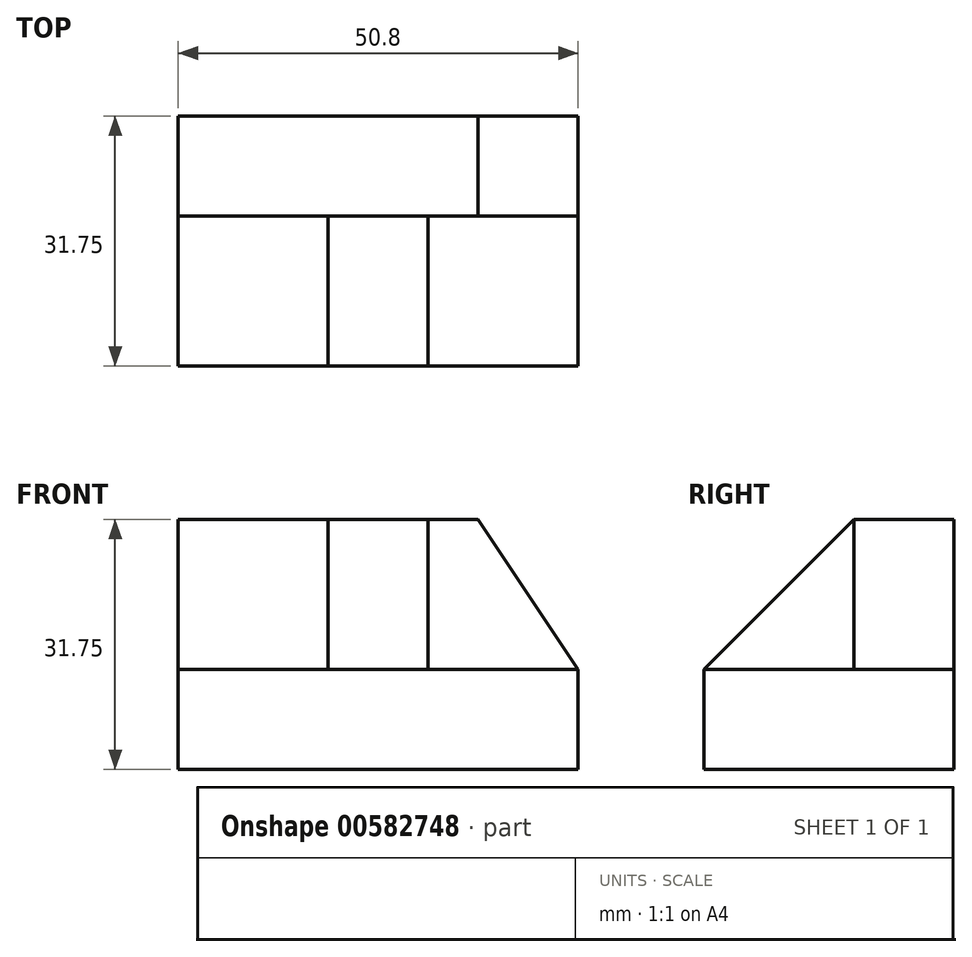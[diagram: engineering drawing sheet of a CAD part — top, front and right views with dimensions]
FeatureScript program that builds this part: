
annotation { "Feature Type Name" : "Feature", "Feature Type Description" : "" }
export const myFeature = defineFeature(function(context is Context, id is Id, definition is map)
    precondition{}
    {
        {
            var Q0;
            Q0=qCreatedBy(makeId("Right.planeOp"),FACE);
            var sketch = newSketch(context, id + "F0", { "sketchPlane" : qUnion([Q0])});
            skLineSegment(sketch, "E0", {"start": v(53.4, 52.7) * mm, "end": v(53.4, 20.95) * mm});
            skLineSegment(sketch, "E1", {"start": v(53.4, 20.95) * mm, "end": v(21.64, 20.95) * mm});
            skLineSegment(sketch, "E2", {"start": v(21.64, 20.95) * mm, "end": v(21.64, 33.65) * mm});
            skLineSegment(sketch, "E3", {"start": v(21.64, 33.65) * mm, "end": v(40.7, 33.65) * mm});
            skLineSegment(sketch, "E4", {"start": v(40.7, 33.65) * mm, "end": v(40.7, 52.7) * mm});
            skLineSegment(sketch, "E5", {"start": v(40.7, 52.7) * mm, "end": v(53.4, 52.7) * mm});
            skSolve(sketch);
        }
        {
            var Q0;
            Q0 = qSketchRegion(id + "F0", true);
            extrude(context, id + "F1", {"entities" : qUnion([Q0]), "depth" : 50.8 * mm, "offsetDistance" : 25.4 * mm});
        }
        {
            var Q0;
            Q0=makeQuery(id+"F1.opExtrude","SWEPT_FACE",FACE,{"disambiguationData":[OSD([sQuery(id+"F0.wireOp",EDGE,"E4")])]});
            var sketch = newSketch(context, id + "F2", { "sketchPlane" : qUnion([Q0])});
            skLineSegment(sketch, "E6", {"start": v(38.1, 52.7) * mm, "end": v(50.8, 33.65) * mm});
            skLineSegment(sketch, "E7", {"start": v(50.8, 33.65) * mm, "end": v(50.8, 52.7) * mm});
            skLineSegment(sketch, "E8", {"start": v(50.8, 52.7) * mm, "end": v(38.1, 52.7) * mm});
            skSolve(sketch);
        }
        {
            var Q0;
            Q0 = qSketchRegion(id + "F2", true);
            extrude(context, id + "F3", {"entities" : qUnion([Q0]), "operationType" : NewBodyOperationType.REMOVE, "oppositeDirection" : true, "depth" : 12.7 * mm, "offsetDistance" : 25.4 * mm});
        }
        {
            var Q0;
            Q0=makeQuery(id+"F1.opExtrude","CAP_FACE",FACE,{"disambiguationData":[OSD([sQuery(id+"F0.wireOp",EDGE,"E0"),sQuery(id+"F0.wireOp",EDGE,"E1"),sQuery(id+"F0.wireOp",EDGE,"E2"),sQuery(id+"F0.wireOp",EDGE,"E3"),sQuery(id+"F0.wireOp",EDGE,"E4"),sQuery(id+"F0.wireOp",EDGE,"E5")])],"isStart":true});
            var sketch = newSketch(context, id + "F4", { "sketchPlane" : qUnion([Q0])});
            skLineSegment(sketch, "E9", {"start": v(-40.7, 52.7) * mm, "end": v(-21.64, 33.65) * mm});
            skLineSegment(sketch, "E10", {"start": v(-21.64, 33.65) * mm, "end": v(-40.7, 33.65) * mm});
            skLineSegment(sketch, "E11", {"start": v(-40.7, 33.65) * mm, "end": v(-40.7, 52.7) * mm});
            skSolve(sketch);
        }
        {
            var Q0;
            Q0 = qSketchRegion(id + "F4", true);
            extrude(context, id + "F5", {"entities" : qUnion([Q0]), "oppositeDirection" : true, "depth" : 31.75 * mm, "offsetDistance" : 25.4 * mm});
        }
        {
            var Q0;
            Q0=makeQuery(id+"F5.opExtrude","CAP_FACE",FACE,{"disambiguationData":[OSD([sQuery(id+"F4.wireOp",EDGE,"E9"),sQuery(id+"F4.wireOp",EDGE,"E10"),sQuery(id+"F4.wireOp",EDGE,"E11")])],"isStart":true});
            var sketch = newSketch(context, id + "F6", { "sketchPlane" : qUnion([Q0])});
            skLineSegment(sketch, "E12", {"start": v(-40.7, 52.7) * mm, "end": v(-40.7, 33.65) * mm});
            skLineSegment(sketch, "E13", {"start": v(-40.7, 33.65) * mm, "end": v(-21.64, 33.65) * mm});
            skLineSegment(sketch, "E14", {"start": v(-21.64, 33.65) * mm, "end": v(-40.7, 52.7) * mm});
            skSolve(sketch);
        }
        {
            var Q0;
            Q0 = qSketchRegion(id + "F6", true);
            extrude(context, id + "F7", {"entities" : qUnion([Q0]), "operationType" : NewBodyOperationType.REMOVE, "oppositeDirection" : true, "depth" : 19.05 * mm, "offsetDistance" : 25.4 * mm});
        }
    });
